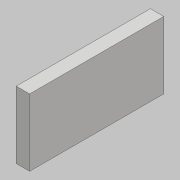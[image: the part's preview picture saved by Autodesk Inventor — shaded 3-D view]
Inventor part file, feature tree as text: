
AUTODESK INVENTOR PART (.ipt)
format: ipt  version: 2018 (Build 220112000, 112)  size: 71,680 bytes
history: native  units: mm
features: other x1, extrude x1, sketch x1
ambient origin geometry x8: Origin, YZ Plane, XZ Plane, XY Plane, X Axis, Y Axis, Z Axis, Center Point
bodies: Body1 (feature_tree)
feature tree (3):
  other  "實體1"
  extrude  "擠出1"  Depth=120.0mm
  sketch  "草圖1"
